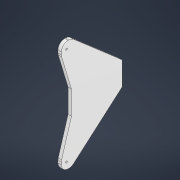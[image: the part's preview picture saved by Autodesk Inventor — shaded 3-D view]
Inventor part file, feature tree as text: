
AUTODESK INVENTOR PART (.ipt)
format: ipt  version: 2022 (Build 260153000, 153)  size: 131,584 bytes
history: native  units: mm
features: extrude x2, sketch x2, other x1, fillet x1, mirror x1
ambient origin geometry x8: Origin, YZ Plane, XZ Plane, XY Plane, X Axis, Y Axis, Z Axis, Center Point
bodies: Body1 (feature_tree)
feature tree (7):
  other  "ソリッド1"
  extrude  "押し出し1"  Depth=1.0mm
  extrude  "押し出し2"  Depth=15.0mm
  fillet  "フィレット1"  Radius=3.5mm
  mirror  "ミラー1"
  sketch  "スケッチ1"
  sketch  "スケッチ2"
